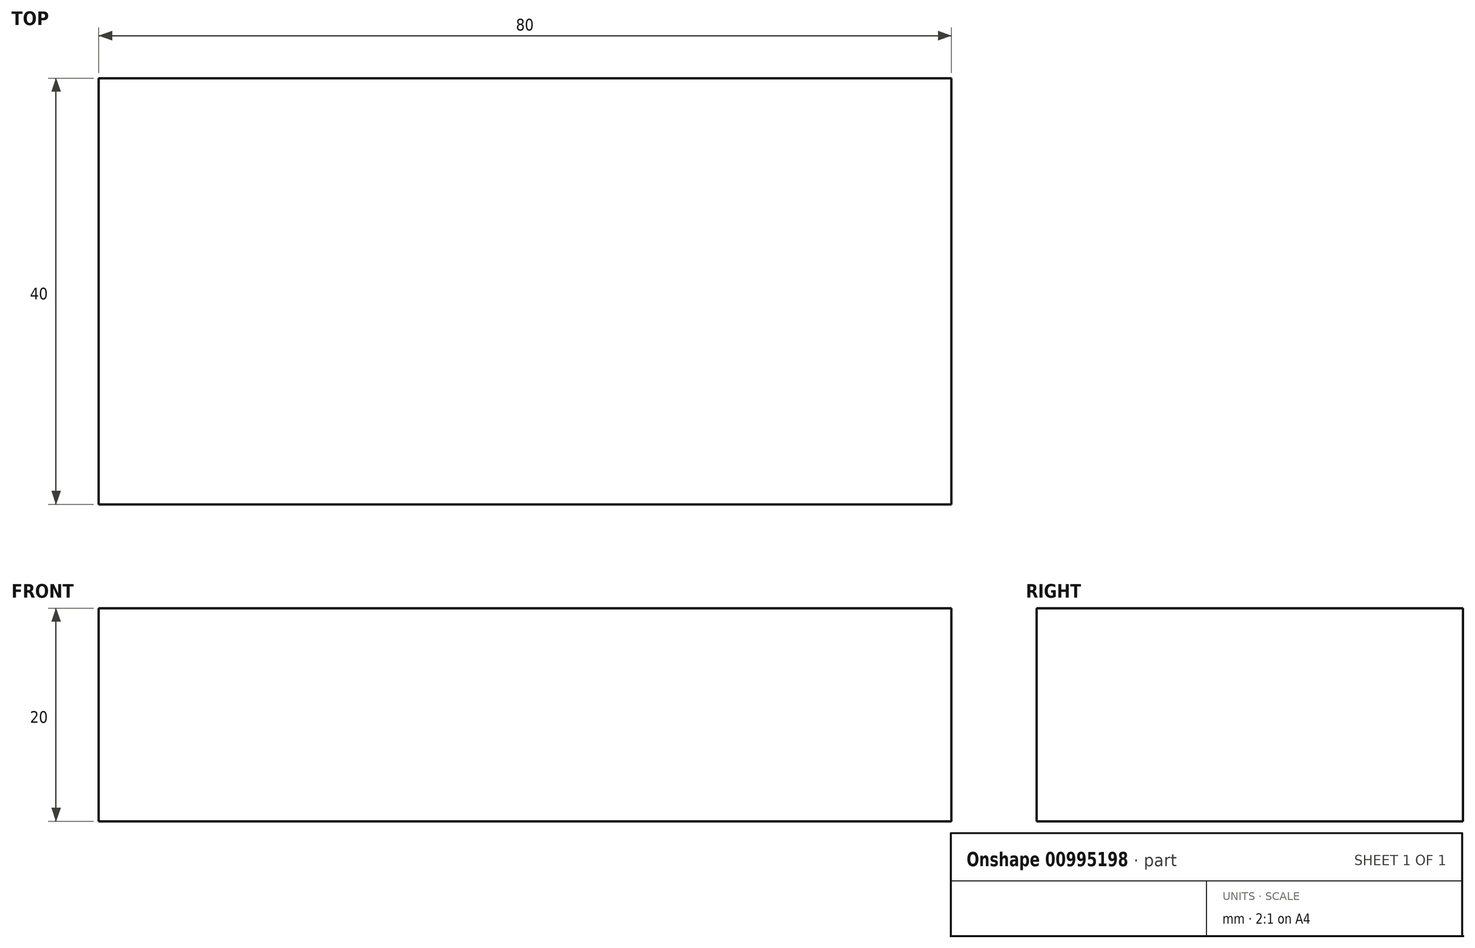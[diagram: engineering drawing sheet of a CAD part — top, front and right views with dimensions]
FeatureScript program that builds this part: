
annotation { "Feature Type Name" : "Feature", "Feature Type Description" : "" }
export const myFeature = defineFeature(function(context is Context, id is Id, definition is map)
    precondition{}
    {
        {
            var Q0;
            Q0=qCreatedBy(makeId("Top.planeOp"),FACE);
            var sketch = newSketch(context, id + "F0", { "sketchPlane" : qUnion([Q0])});
            skLineSegment(sketch, "E0.bottom", {"start": v(0, 0) * mm, "end": v(80, 0) * mm});
            skLineSegment(sketch, "E0.top", {"start": v(0, 40) * mm, "end": v(80, 40) * mm});
            skLineSegment(sketch, "E0.left", {"start": v(0, 0) * mm, "end": v(0, 40) * mm});
            skLineSegment(sketch, "E0.right", {"start": v(80, 0) * mm, "end": v(80, 40) * mm});
            skSolve(sketch);
        }
        {
            var Q0;
            Q0=makeQuery(id+"F0.imprint","IMPRINT",FACE,{"disambiguationData":[TD([[makeQuery(id+"F0.imprint","IMPRINT",EDGE,{"derivedFrom":sQuery(id+"F0.wireOp",EDGE,"E0.bottom")}),1.0]])]});
            extrude(context, id + "F1", {"entities" : qUnion([Q0]), "depth" : 20 * mm, "offsetDistance" : 25 * mm});
        }
    });
